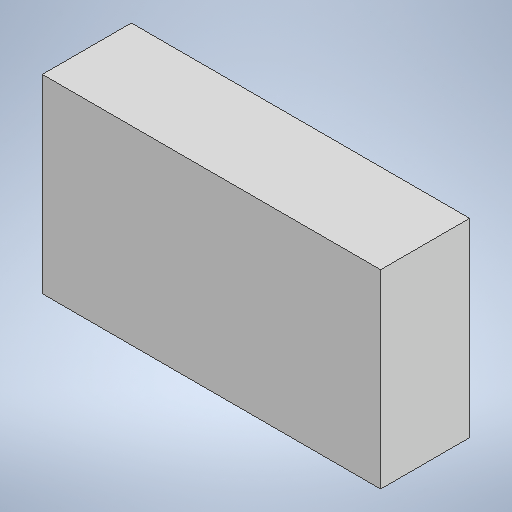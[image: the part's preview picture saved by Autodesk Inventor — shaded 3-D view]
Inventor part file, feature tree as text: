
AUTODESK INVENTOR PART (.ipt)
format: ipt  version: 2025.1 (Build 291241000, 241)  size: 173,568 bytes
history: native  units: mm
features: other x1, extrude x1, sketch x1
ambient origin geometry x8: Origin, YZ Plane, XZ Plane, XY Plane, X Axis, Y Axis, Z Axis, Center Point
bodies: Body1 (feature_tree)
feature tree (3):
  other  "ソリッド1"
  extrude  "押し出し1"  Depth=57.0mm
  sketch  "スケッチ1"
